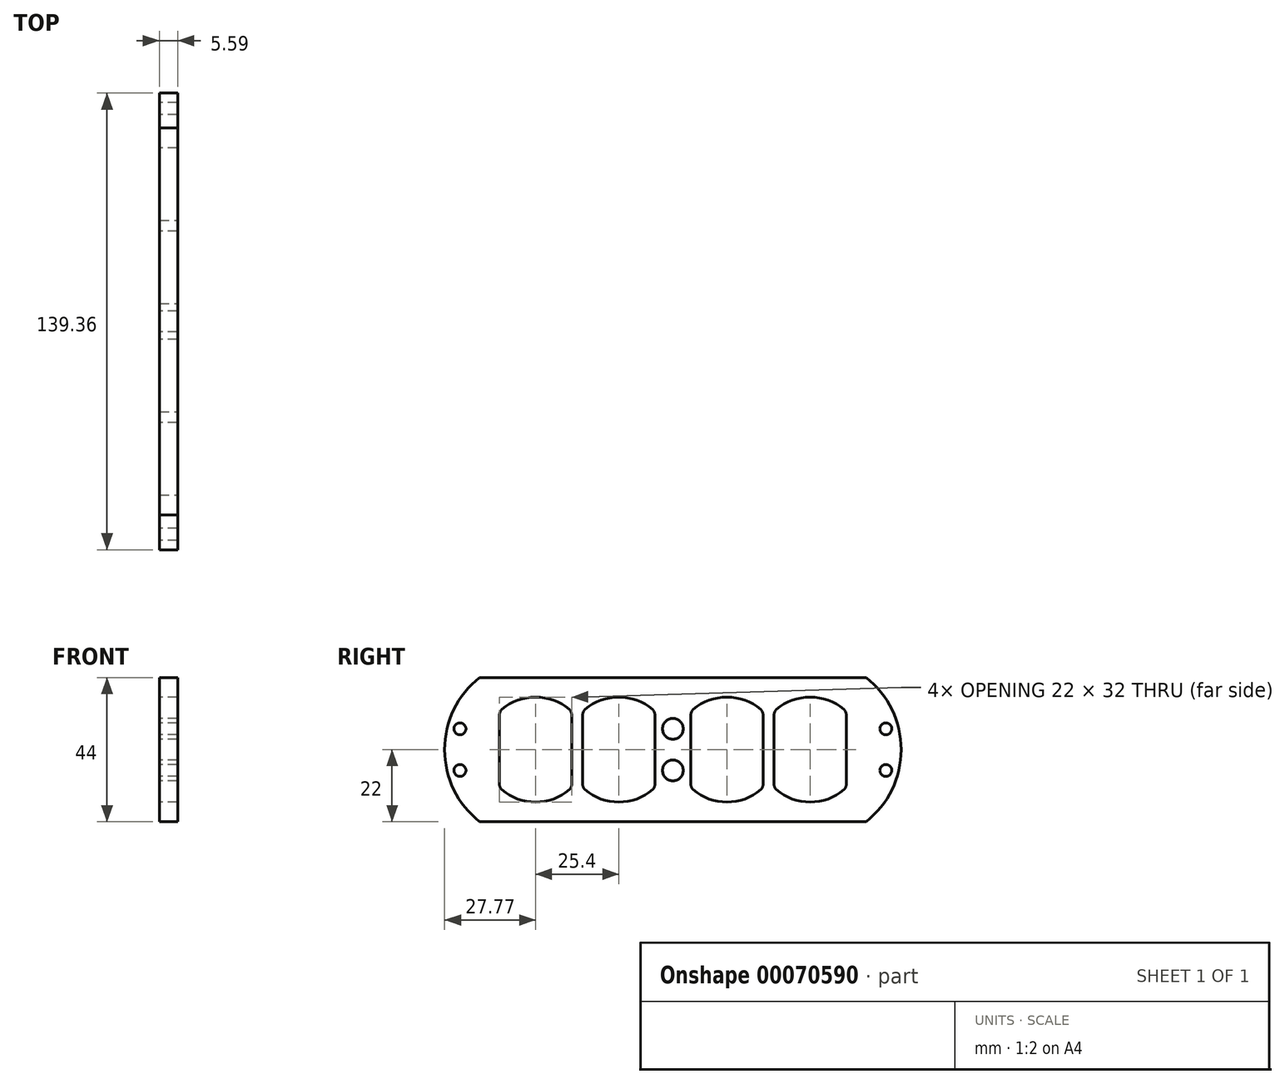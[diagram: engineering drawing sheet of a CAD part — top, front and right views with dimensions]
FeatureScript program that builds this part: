
annotation { "Feature Type Name" : "Feature", "Feature Type Description" : "" }
export const myFeature = defineFeature(function(context is Context, id is Id, definition is map)
    precondition{}
    {
        {
            var Q0;
            Q0=qCreatedBy(makeId("Right.planeOp"),FACE);
            var sketch = newSketch(context, id + "F0", { "sketchPlane" : qUnion([Q0])});
            skLineSegment(sketch, "E0.rect.bottom", {"start": v(59, 22) * mm, "end": v(-59, 22) * mm});
            skLineSegment(sketch, "E0.rect.top", {"start": v(59, -22) * mm, "end": v(-59, -22) * mm});
            skLineSegment(sketch, "E0.rect.left", {"start": v(59, 22) * mm, "end": v(59, -22) * mm, "construction": true});
            skLineSegment(sketch, "E0.rect.right", {"start": v(-59, 22) * mm, "end": v(-59, -22) * mm, "construction": true});
            skPoint(sketch, "E0.rect.middle", {"position": v(0, 0) * mm});
            skLineSegment(sketch, "E1", {"start": v(-59, 0) * mm, "end": v(59, 0) * mm, "construction": true});
            skArc(sketch, "E2", {"start": v(-52.9, -11.62) * mm, "mid": v(-41.91, -16) * mm, "end": v(-30.91, -11.62) * mm});
            skArc(sketch, "E3", {"start": v(-5.51, 11.62) * mm, "mid": v(-16.5, 16) * mm, "end": v(-27.5, 11.62) * mm});
            skArc(sketch, "E4", {"start": v(5.51, -11.62) * mm, "mid": v(16.51, -16) * mm, "end": v(27.5, -11.62) * mm});
            skArc(sketch, "E5", {"start": v(30.91, -11.62) * mm, "mid": v(41.91, -16) * mm, "end": v(52.9, -11.62) * mm});
            skLineSegment(sketch, "E6.rect.bottom", {"start": v(-5.5, 11.62) * mm, "end": v(-27.51, 11.62) * mm, "construction": true});
            skLineSegment(sketch, "E6.rect.top", {"start": v(-5.5, -11.62) * mm, "end": v(-27.51, -11.62) * mm, "construction": true});
            skLineSegment(sketch, "E6.rect.left", {"start": v(-5.5, 11.62) * mm, "end": v(-5.5, -11.62) * mm});
            skLineSegment(sketch, "E6.rect.right", {"start": v(-27.51, 11.62) * mm, "end": v(-27.51, -11.62) * mm});
            skLineSegment(sketch, "E7.rect.bottom", {"start": v(-30.91, 11.62) * mm, "end": v(-52.9, 11.62) * mm, "construction": true});
            skLineSegment(sketch, "E7.rect.top", {"start": v(-30.91, -11.62) * mm, "end": v(-52.9, -11.62) * mm, "construction": true});
            skLineSegment(sketch, "E7.rect.left", {"start": v(-30.91, 11.62) * mm, "end": v(-30.91, -11.62) * mm});
            skLineSegment(sketch, "E7.rect.right", {"start": v(-52.91, 11.62) * mm, "end": v(-52.91, -11.62) * mm});
            skLineSegment(sketch, "E8.rect.bottom", {"start": v(27.51, 11.62) * mm, "end": v(5.51, 11.62) * mm, "construction": true});
            skLineSegment(sketch, "E8.rect.top", {"start": v(27.51, -11.62) * mm, "end": v(5.51, -11.62) * mm, "construction": true});
            skLineSegment(sketch, "E8.rect.left", {"start": v(27.51, 11.62) * mm, "end": v(27.51, -11.62) * mm});
            skLineSegment(sketch, "E8.rect.right", {"start": v(5.51, 11.62) * mm, "end": v(5.51, -11.62) * mm});
            skLineSegment(sketch, "E9.rect.bottom", {"start": v(52.91, 11.62) * mm, "end": v(30.91, 11.62) * mm, "construction": true});
            skLineSegment(sketch, "E9.rect.top", {"start": v(52.91, -11.62) * mm, "end": v(30.91, -11.62) * mm, "construction": true});
            skLineSegment(sketch, "E9.rect.left", {"start": v(52.91, 11.62) * mm, "end": v(52.91, -11.62) * mm});
            skLineSegment(sketch, "E9.rect.right", {"start": v(30.91, 11.62) * mm, "end": v(30.91, -11.62) * mm});
            skArc(sketch, "E10.trimOffspring", {"start": v(27.51, 11.62) * mm, "mid": v(16.51, 16) * mm, "end": v(5.51, 11.62) * mm});
            skArc(sketch, "E11.trimOffspring", {"start": v(52.91, 11.62) * mm, "mid": v(41.91, 16) * mm, "end": v(30.9, 11.62) * mm});
            skArc(sketch, "E12.trimOffspring", {"start": v(-27.51, -11.62) * mm, "mid": v(-16.51, -16) * mm, "end": v(-5.5, -11.62) * mm});
            skArc(sketch, "E13.trimOffspring", {"start": v(-30.91, 11.62) * mm, "mid": v(-41.91, 16) * mm, "end": v(-52.9, 11.62) * mm});
            skCircle(sketch, "E14", {"center": v(0, 6.35) * mm, "radius": 3.18 * mm});
            skCircle(sketch, "E15", {"center": v(0, -6.35) * mm, "radius": 3.18 * mm});
            skLineSegment(sketch, "E16", {"start": v(0, 6.35) * mm, "end": v(0, -6.35) * mm, "construction": true});
            skArc(sketch, "E17", {"start": v(59, -22) * mm, "mid": v(69.68, 0) * mm, "end": v(59, 22) * mm});
            skCircle(sketch, "E18", {"center": v(-65, -6.35) * mm, "radius": 1.83 * mm});
            skCircle(sketch, "E19", {"center": v(65, -6.35) * mm, "radius": 1.83 * mm});
            skArc(sketch, "E20", {"start": v(-59, 22) * mm, "mid": v(-69.68, 0) * mm, "end": v(-59, -22) * mm});
            skCircle(sketch, "E21", {"center": v(-65, 6.35) * mm, "radius": 1.83 * mm});
            skCircle(sketch, "E22", {"center": v(65, 6.35) * mm, "radius": 1.83 * mm});
            skLineSegment(sketch, "E23", {"start": v(-65, 6.35) * mm, "end": v(-65, -6.35) * mm, "construction": true});
            skLineSegment(sketch, "E24", {"start": v(-59, 0) * mm, "end": v(-65, 0) * mm, "construction": true});
            skSolve(sketch);
        }
        {
            var Q0;
            Q0=makeQuery(id+"F0.imprint","IMPRINT",FACE,{"disambiguationData":[TD([[makeQuery(id+"F0.imprint","IMPRINT",EDGE,{"derivedFrom":sQuery(id+"F0.wireOp",EDGE,"E0.rect.bottom")}),1.0]])]});
            extrude(context, id + "F1", {"entities" : qUnion([Q0]), "depth" : 5.6 * mm});
        }
        {
            var Q0;
            Q0=makeQuery(id+"F1.opExtrude","SWEPT_EDGE",EDGE,{"disambiguationData":[OSD([sQuery(id+"F0.wireOp",EDGE,"E3"),sQuery(id+"F0.wireOp",EDGE,"E13.trimOffspring")])]});
            var Q1;
            Q1=makeQuery(id+"F1.opExtrude","SWEPT_EDGE",EDGE,{"disambiguationData":[OSD([sQuery(id+"F0.wireOp",EDGE,"E3"),sQuery(id+"F0.wireOp",EDGE,"E6.rect.bottom"),sQuery(id+"F0.wireOp",EDGE,"E6.rect.left")])]});
            var Q2;
            Q2=makeQuery(id+"F1.opExtrude","SWEPT_EDGE",EDGE,{"disambiguationData":[OSD([sQuery(id+"F0.wireOp",EDGE,"E10.trimOffspring"),sQuery(id+"F0.wireOp",EDGE,"E11.trimOffspring")])]});
            var Q3;
            Q3=makeQuery(id+"F1.opExtrude","SWEPT_EDGE",EDGE,{"disambiguationData":[OSD([sQuery(id+"F0.wireOp",EDGE,"E9.rect.bottom"),sQuery(id+"F0.wireOp",EDGE,"E9.rect.left"),sQuery(id+"F0.wireOp",EDGE,"E11.trimOffspring")])]});
            var Q4;
            Q4=makeQuery(id+"F1.opExtrude","SWEPT_EDGE",EDGE,{"disambiguationData":[OSD([sQuery(id+"F0.wireOp",EDGE,"e33f25ae-1f6d-40e0-9dec-565fcb922949"),sQuery(id+"F0.wireOp",EDGE,"5de0432f-1205-4019-b9fe-66099e7e3eea.trimOffspring")])]});
            var Q5;
            Q5=makeQuery(id+"F1.opExtrude","SWEPT_EDGE",EDGE,{"disambiguationData":[OSD([sQuery(id+"F0.wireOp",EDGE,"e33f25ae-1f6d-40e0-9dec-565fcb922949"),sQuery(id+"F0.wireOp",EDGE,"5e5a8d91-dd87-4eb5-9441-2014a3c203cb.rect.bottom"),sQuery(id+"F0.wireOp",EDGE,"5e5a8d91-dd87-4eb5-9441-2014a3c203cb.rect.left")])]});
            var Q6;
            Q6=makeQuery(id+"F1.opExtrude","SWEPT_EDGE",EDGE,{"disambiguationData":[OSD([sQuery(id+"F0.wireOp",EDGE,"3900715f-9ec9-427c-b40c-1b29114f17ff"),sQuery(id+"F0.wireOp",EDGE,"87819232-e227-4609-b230-a19b5395fd35.trimOffspring")])]});
            var Q7;
            Q7=makeQuery(id+"F1.opExtrude","SWEPT_EDGE",EDGE,{"disambiguationData":[OSD([sQuery(id+"F0.wireOp",EDGE,"3900715f-9ec9-427c-b40c-1b29114f17ff"),sQuery(id+"F0.wireOp",EDGE,"b878eb50-c1ad-4fd4-9c69-5f7b8b37a9d8.rect.top"),sQuery(id+"F0.wireOp",EDGE,"b878eb50-c1ad-4fd4-9c69-5f7b8b37a9d8.rect.right")])]});
            var Q8;
            Q8=makeQuery(id+"F1.opExtrude","SWEPT_EDGE",EDGE,{"disambiguationData":[OSD([sQuery(id+"F0.wireOp",EDGE,"b878eb50-c1ad-4fd4-9c69-5f7b8b37a9d8.rect.bottom"),sQuery(id+"F0.wireOp",EDGE,"b878eb50-c1ad-4fd4-9c69-5f7b8b37a9d8.rect.right"),sQuery(id+"F0.wireOp",EDGE,"5de0432f-1205-4019-b9fe-66099e7e3eea.trimOffspring")])]});
            var Q9;
            Q9=makeQuery(id+"F1.opExtrude","SWEPT_EDGE",EDGE,{"disambiguationData":[OSD([sQuery(id+"F0.wireOp",EDGE,"E4"),sQuery(id+"F0.wireOp",EDGE,"E5")])]});
            var Q10;
            Q10=makeQuery(id+"F1.opExtrude","SWEPT_EDGE",EDGE,{"disambiguationData":[OSD([sQuery(id+"F0.wireOp",EDGE,"E4"),sQuery(id+"F0.wireOp",EDGE,"E8.rect.top"),sQuery(id+"F0.wireOp",EDGE,"E8.rect.right")])]});
            var Q11;
            Q11=makeQuery(id+"F1.opExtrude","SWEPT_EDGE",EDGE,{"disambiguationData":[OSD([sQuery(id+"F0.wireOp",EDGE,"E8.rect.bottom"),sQuery(id+"F0.wireOp",EDGE,"E8.rect.right"),sQuery(id+"F0.wireOp",EDGE,"E10.trimOffspring")])]});
            var Q12;
            Q12=makeQuery(id+"F1.opExtrude","SWEPT_EDGE",EDGE,{"disambiguationData":[OSD([sQuery(id+"F0.wireOp",EDGE,"E2"),sQuery(id+"F0.wireOp",EDGE,"E12.trimOffspring")])]});
            var Q13;
            Q13=makeQuery(id+"F1.opExtrude","SWEPT_EDGE",EDGE,{"disambiguationData":[OSD([sQuery(id+"F0.wireOp",EDGE,"E2"),sQuery(id+"F0.wireOp",EDGE,"E7.rect.top"),sQuery(id+"F0.wireOp",EDGE,"E7.rect.right")])]});
            var Q14;
            Q14=makeQuery(id+"F1.opExtrude","SWEPT_EDGE",EDGE,{"disambiguationData":[OSD([sQuery(id+"F0.wireOp",EDGE,"E7.rect.bottom"),sQuery(id+"F0.wireOp",EDGE,"E7.rect.right"),sQuery(id+"F0.wireOp",EDGE,"E13.trimOffspring")])]});
            var Q15;
            Q15=makeQuery(id+"F1.opExtrude","SWEPT_EDGE",EDGE,{"disambiguationData":[OSD([sQuery(id+"F0.wireOp",EDGE,"E6.rect.top"),sQuery(id+"F0.wireOp",EDGE,"E6.rect.left"),sQuery(id+"F0.wireOp",EDGE,"E12.trimOffspring")])]});
            var Q16;
            Q16=makeQuery(id+"F1.opExtrude","SWEPT_EDGE",EDGE,{"disambiguationData":[OSD([sQuery(id+"F0.wireOp",EDGE,"E5"),sQuery(id+"F0.wireOp",EDGE,"E9.rect.top"),sQuery(id+"F0.wireOp",EDGE,"E9.rect.left")])]});
            var Q17;
            Q17=makeQuery(id+"F1.opExtrude","SWEPT_EDGE",EDGE,{"disambiguationData":[OSD([sQuery(id+"F0.wireOp",EDGE,"5e5a8d91-dd87-4eb5-9441-2014a3c203cb.rect.top"),sQuery(id+"F0.wireOp",EDGE,"5e5a8d91-dd87-4eb5-9441-2014a3c203cb.rect.left"),sQuery(id+"F0.wireOp",EDGE,"87819232-e227-4609-b230-a19b5395fd35.trimOffspring")])]});
            fillet(context, id + "F2", {"entities" : qUnion([Q0, Q1, Q2, Q3, Q4, Q5, Q6, Q7, Q8, Q9, Q10, Q11, Q12, Q13, Q14, Q15, Q16, Q17]), "radius" : 2 * mm, "tangentPropagation" : true, "allowEdgeOverflow" : false});
        }
    });
